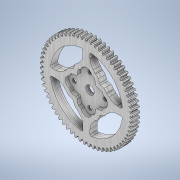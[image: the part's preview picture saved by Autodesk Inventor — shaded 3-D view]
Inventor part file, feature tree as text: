
AUTODESK INVENTOR PART (.ipt)
format: ipt  version: 2020.2 (Build 242310000, 310)  size: 2,085,376 bytes
history: native  units: mm
features: extrude x5, sketch x5, other x4, fillet x3, hole x1, chamfer x1, projected_geometry x1
ambient origin geometry x8: Origin, YZ Plane, XZ Plane, XY Plane, X Axis, Y Axis, Z Axis, Center Point
bodies: Body1 (feature_tree)
feature tree (20):
  other  "ソリッド1"
  extrude  "押し出し1"  Depth=5.0mm TaperAngle=0.0deg
  sketch  "スケッチ2"
  extrude  "押し出し2"  Depth=10.0mm TaperAngle=0.0deg
  extrude  "押し出し3"  Depth=10.0mm TaperAngle=0.0deg
  extrude  "押し出し4"  Depth=2.5mm TaperAngle=0.0deg
  hole  "穴1"  [1 undecoded]
  chamfer  "面取り1"  Distance=0.5mm
  sketch  "スケッチ4"
  fillet  "フィレット1"  Radius=3.0mm
  extrude  "押し出し5"  Depth=5.0mm
  fillet  "フィレット2"  Radius=5.0mm
  fillet  "フィレット3"  Radius=5.0mm
  sketch  "スケッチ1"
  sketch  "スケッチ3"
  projected_geometry  "投影ループ1"
  sketch  "スケッチ5"
  other  "断面エッジを投影1"
  other  "断面エッジを投影2"
  other  "断面エッジを投影3"
note: 1 required parameter value undecoded (feature->parameter linkage not recoverable at this tier; creation-order binding heuristic only, values carry confidence <= 0.55)
